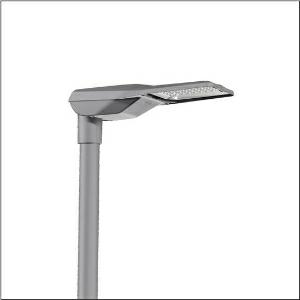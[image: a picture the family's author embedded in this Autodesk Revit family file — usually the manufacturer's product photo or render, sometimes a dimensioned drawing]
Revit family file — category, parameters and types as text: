
# Revit family: streetlight_sl_21_mini___pl52_5xe6h33a08gb_e896
name_source: partatom
category: Lighting Fixtures
units: mm (PartAtom-declared; Revit-internal decimal feet)

## family parameters
Cut with Voids When Loaded = No
Host = Face
Light Source = No
Part Type = Normal
Room Calculation Point = No
Round Connector Dimension = Use Diameter
Shared = No

## types (1)
- --- (1 x LED, 5840 lm, 40.4 W, 3000K)
    Apparent Load = 40 VA
    CIE Flux Codes = 27 59 98 100 100
    Color Rendering = 70
    Color Temperature = 3000K
    Default Elevation = 1800 mm
    Description = Streetlight SL 21 mini, mast luminaire, primary light control with lens, of PMMA, primary optical cover: cover, of toughened safety glass, transparent, light distribution: PL52, light emission: direct distribution, primary light characteristic: asymmetric, installation type: post-top, side-entry, LED, 2X 1.5mm², High Power LED, rated luminous flux: 5.840lm, luminous efficacy: 145lm/W, light colour: 730, colour temperature: 3000K, control gear: Easy, control: overheat protection, constant luminous flux control, time-dependent luminous flux control, flexible luminous flux parameterisation, mains connection: 230..240V, AC, 50/60Hz, connection cable pre-assembled, cable length: 6,5m, wiring characteristics: H07RN-F, start of lifetime: 40W, end of service life: 41W, reduction: 19W, luminaire housing, of diecast aluminium, powder-coated, SITECO metallic grey (DB 702S), corrosivity category C5 high according to DIN EN ISO 12944, please order mast flange separately, inclination adjustable: 0°, 5°, 10°, 15°, sealing non-destructively replaceable, multi-level sealing system, length: 628mm, width: 235mm, height: 110mm, mast flange for spigot size: 42mm (side-entry): 5XC10008XM4, 60/48mm (side-entry/post-top): 5XC10108XM2, 76/60mm (side-entry/post-top): 5XC10108XM1, mounting height: 4..8m, protection rating (complete): IP66, insulation class (complete): insulation class II (safety insulation), certification: CE, ENEC, ENEC+, VDE, impact resistance: IK10, permissible operating ambient temperature for outdoor applications: -40..+50°C, standard-compliant lighting for roads and squares, packaging unit: 1 piece

Light Distribution: PL52
    Height = 110 mm
    Lamp = 1 x LED
    Lamp Light Flux = 5840 lm
    Lamp Power = 40.4 W
    Lamp count = 1
    Length = 625 mm
    Luminous efficacy = 145 lm/W
    Manufacturer = Siteco
    ModVariant = No
    Model = 5XE6H33A08GB
    Number of Poles = 1
    OnlyDefault = Yes
    Power Factor = 1
    Product Name = Streetlight SL 21 mini | PL52
    Product group = mast luminaire | pylon top
    ProductGroupID = 6100
    Protection Class = Protection class II
    Protection Degree = IP 66
    RLX_Detail_Level = 1
    RLX_Emergency_Light_Flux = 0 lm
    RLX_Emergency_Type = 0
    RLX_Emergency_Type_DB = No
    RlxData = <blob elided: 35485 chars, md5=6227ae0f>
    Socket = socket
    Standby Power = 0 W
    System Light Flux = 5840 lm
    System Power = 40 W
    Type Comments = factory setting: luminous flux: 100 % | Output Level: 100 % | 812 mA
    Type Image = l_1003519.jpg
    URL = http://relux.com
    VarID = @adj_187375
    Voltage = 0 V
    Weight = 0.00 kg
    Width = 234 mm

## geometry (parser evidence)
native form markers: Blend x4, Sweep x10
no freeform markers — native parametric forms only
